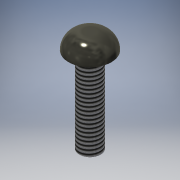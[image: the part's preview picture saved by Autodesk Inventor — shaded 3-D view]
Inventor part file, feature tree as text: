
AUTODESK INVENTOR PART (.ipt)
format: ipt  version: 2020.2 (Build 242310000, 310)  size: 140,800 bytes
history: native  units: mm
features: extrude x3, sketch x3, other x1, fillet x1, thread x1
ambient origin geometry x1: Origin
bodies: Body1 (feature_tree)
feature tree (9):
  other  "ソリッド1"
  extrude  "押し出し1"  Depth=4.0mm
  extrude  "押し出し2"  Depth=6.0mm TaperAngle=0.0deg
  fillet  "フィレット1"  Radius=8.0mm
  thread  "ねじ1"
  extrude  "押し出し3"  Depth=3.0mm TaperAngle=0.0deg
  sketch  "スケッチ1"
  sketch  "スケッチ2"
  sketch  "スケッチ3"
